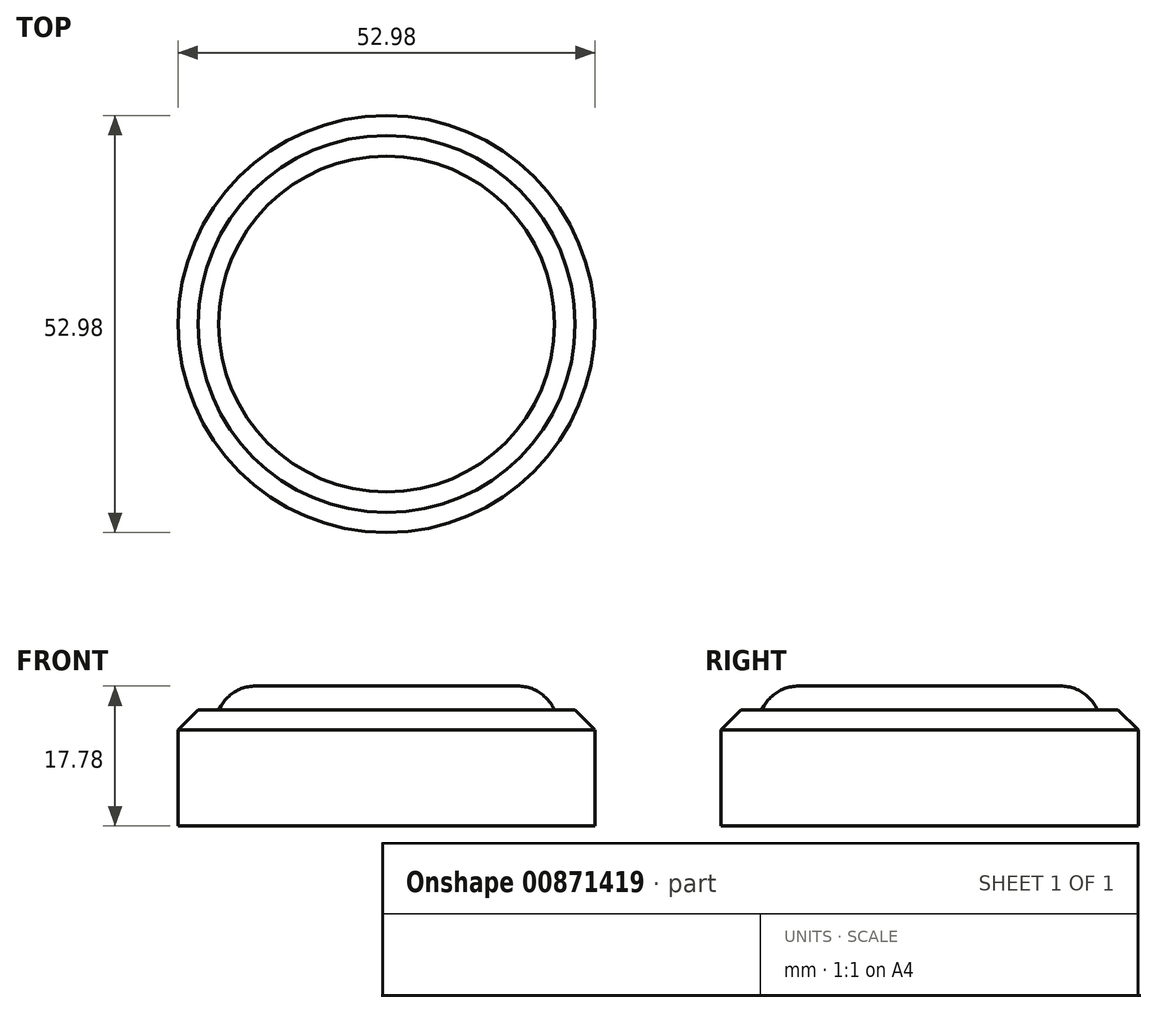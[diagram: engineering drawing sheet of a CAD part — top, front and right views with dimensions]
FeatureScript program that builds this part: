
annotation { "Feature Type Name" : "Feature", "Feature Type Description" : "" }
export const myFeature = defineFeature(function(context is Context, id is Id, definition is map)
    precondition{}
    {
        {
            var Q0;
            Q0=qCreatedBy(makeId("Top.planeOp"),FACE);
            var sketch = newSketch(context, id + "F0", { "sketchPlane" : qUnion([Q0])});
            skCircle(sketch, "E0", {"center": v(0, 0) * mm, "radius": 26.49 * mm});
            skSolve(sketch);
        }
        {
            var Q0;
            Q0=makeQuery(id+"F0.imprint","IMPRINT",FACE,{"disambiguationData":[TD([[makeQuery(id+"F0.imprint","IMPRINT",EDGE,{"derivedFrom":sQuery(id+"F0.wireOp",EDGE,"E0")}),1.0]])]});
            extrude(context, id + "F1", {"entities" : qUnion([Q0]), "depth" : 14.73 * mm, "offsetDistance" : 25.4 * mm});
        }
        {
            var Q0;
            Q0=makeQuery(id+"F1.opExtrude","CAP_EDGE",EDGE,{"disambiguationData":[OSD([sQuery(id+"F0.wireOp",EDGE,"E0")])],"isStart":false});
            chamfer(context, id + "F2", {"entities" : qUnion([Q0]), "width" : 2.54 * mm, "tangentPropagation" : true});
        }
        {
            var Q0;
            Q0=makeQuery(id+"F1.opExtrude","CAP_FACE",FACE,{"disambiguationData":[OSD([sQuery(id+"F0.wireOp",EDGE,"E0")])],"isStart":false});
            var sketch = newSketch(context, id + "F3", { "sketchPlane" : qUnion([Q0])});
            skCircle(sketch, "E1", {"center": v(0, 0) * mm, "radius": 21.34 * mm});
            skSolve(sketch);
        }
        {
            var Q0;
            Q0=makeQuery(id+"F3.imprint","IMPRINT",FACE,{"disambiguationData":[TD([[makeQuery(id+"F3.imprint","IMPRINT",EDGE,{"derivedFrom":sQuery(id+"F3.wireOp",EDGE,"E1")}),1.0]])]});
            extrude(context, id + "F4", {"entities" : qUnion([Q0]), "operationType" : NewBodyOperationType.ADD, "depth" : 3.05 * mm, "offsetDistance" : 25.4 * mm, "hasDraft" : true, "draftAngle" : 30 * degree, "draftPullDirection" : true});
        }
        {
            var Q0;
            Q0=makeQuery(id+"F4.opExtrude","CAP_EDGE",EDGE,{"disambiguationData":[OSD([sQuery(id+"F3.wireOp",EDGE,"E1")])],"isStart":false});
            fillet(context, id + "F5", {"entities" : qUnion([Q0]), "radius" : 5.08 * mm, "tangentPropagation" : true, "allowEdgeOverflow" : false});
        }
    });
